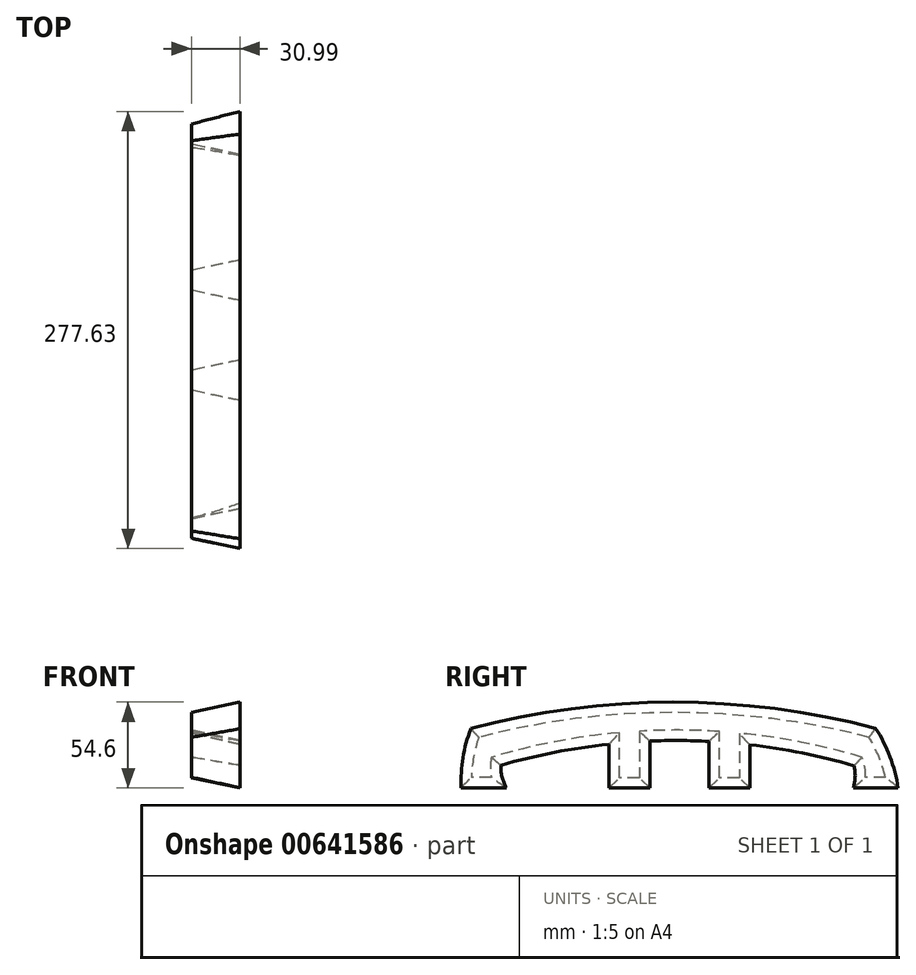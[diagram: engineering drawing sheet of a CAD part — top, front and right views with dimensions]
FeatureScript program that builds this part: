
annotation { "Feature Type Name" : "Feature", "Feature Type Description" : "" }
export const myFeature = defineFeature(function(context is Context, id is Id, definition is map)
    precondition{}
    {
        {
            var Q0;
            Q0=qCreatedBy(makeId("Right.planeOp"),FACE);
            var sketch = newSketch(context, id + "F0", { "sketchPlane" : qUnion([Q0])});
            skArc(sketch, "E0", {"start": v(120.57, -25.32) * mm, "mid": v(-3.34, -9.54) * mm, "end": v(-127.26, -25.32) * mm});
            skArc(sketch, "E1", {"start": v(131.11, -50.72) * mm, "mid": v(126.83, -37.6) * mm, "end": v(120.57, -25.32) * mm});
            skArc(sketch, "E2", {"start": v(-127.26, -25.32) * mm, "mid": v(-130.5, -37.85) * mm, "end": v(-131.88, -50.72) * mm});
            skLineSegment(sketch, "E3", {"start": v(131.11, -50.72) * mm, "end": v(118.41, -50.72) * mm});
            skLineSegment(sketch, "E4", {"start": v(-131.88, -50.72) * mm, "end": v(-119.18, -50.72) * mm});
            skArc(sketch, "E5", {"start": v(118.41, -50.72) * mm, "mid": v(117.96, -44.25) * mm, "end": v(116.21, -38.02) * mm});
            skArc(sketch, "E6", {"start": v(-119.18, -38.02) * mm, "mid": v(-119.82, -44.37) * mm, "end": v(-119.18, -50.72) * mm});
            skArc(sketch, "E7", {"start": v(116.21, -38.02) * mm, "mid": v(77.6, -28.48) * mm, "end": v(38.24, -22.72) * mm});
            skLineSegment(sketch, "E8", {"start": v(38.24, -22.72) * mm, "end": v(38.24, -50.97) * mm});
            skLineSegment(sketch, "E9", {"start": v(38.24, -50.97) * mm, "end": v(25.54, -50.97) * mm});
            skLineSegment(sketch, "E10", {"start": v(25.54, -50.97) * mm, "end": v(25.54, -21.68) * mm});
            skLineSegment(sketch, "E11", {"start": v(-25.26, -21.48) * mm, "end": v(-25.26, -50.97) * mm});
            skLineSegment(sketch, "E12", {"start": v(-25.26, -50.97) * mm, "end": v(-37.96, -50.97) * mm});
            skLineSegment(sketch, "E13", {"start": v(-37.96, -50.97) * mm, "end": v(-37.96, -22.41) * mm});
            skArc(sketch, "E14.trimOffspring", {"start": v(-37.96, -22.41) * mm, "mid": v(-78.96, -28.16) * mm, "end": v(-119.18, -38.02) * mm});
            skArc(sketch, "E15.trimOffspring", {"start": v(25.54, -21.68) * mm, "mid": v(0.15, -20.8) * mm, "end": v(-25.26, -21.48) * mm});
            skSolve(sketch);
        }
        {
            var Q0;
            Q0=makeQuery(id+"F0.imprint","IMPRINT",FACE,{"disambiguationData":[TD([[makeQuery(id+"F0.imprint","IMPRINT",EDGE,{"derivedFrom":sQuery(id+"F0.wireOp",EDGE,"E0")}),1.0]])]});
            extrude(context, id + "F1", {"entities" : qUnion([Q0]), "depth" : 30.99 * mm, "offsetDistance" : 25.4 * mm, "hasDraft" : true, "draftAngle" : 12 * degree});
        }
    });
